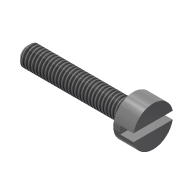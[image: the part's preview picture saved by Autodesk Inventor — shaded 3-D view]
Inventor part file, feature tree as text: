
AUTODESK INVENTOR PART (.ipt)
format: ipt  version: 2015 SP1 (Build 190203100, 203)  size: 104,960 bytes
history: native  units: mm
features: extrude x3, sketch x2, chamfer x1, thread x1, projected_geometry x1
ambient origin geometry x8: Origin, YZ Plane, XZ Plane, XY Plane, X Axis, Y Axis, Z Axis, Center Point
bodies: Solid1 (feature_tree)
feature tree (8):
  sketch  "Sketch1"  dims[d0=3.0mm d1=6.0mm]
  extrude  "Extrusion1"  Depth=3.0mm
  extrude  "Extrusion2"  Depth=3.0mm TaperAngle=0.0deg
  extrude  "Extrusion3"  Depth=2.0mm TaperAngle=0.0deg
  chamfer  "Chamfer1"  Distance=2.0mm Angle=45.0deg
  thread  "Thread2"  [1 undecoded]
  sketch  "Sketch2"  dims[d2=16.0mm d3=0.0mm d4=3.0mm d5=0.0mm d6=2.0mm d7=0.0mm d10=0.5mm d11=2.0mm d12=45.0deg d13=5.0mm d14=0.0mm]
  projected_geometry  "Projected Loop1"
note: 1 required parameter value undecoded (feature->parameter linkage not recoverable at this tier; creation-order binding heuristic only, values carry confidence <= 0.55)
